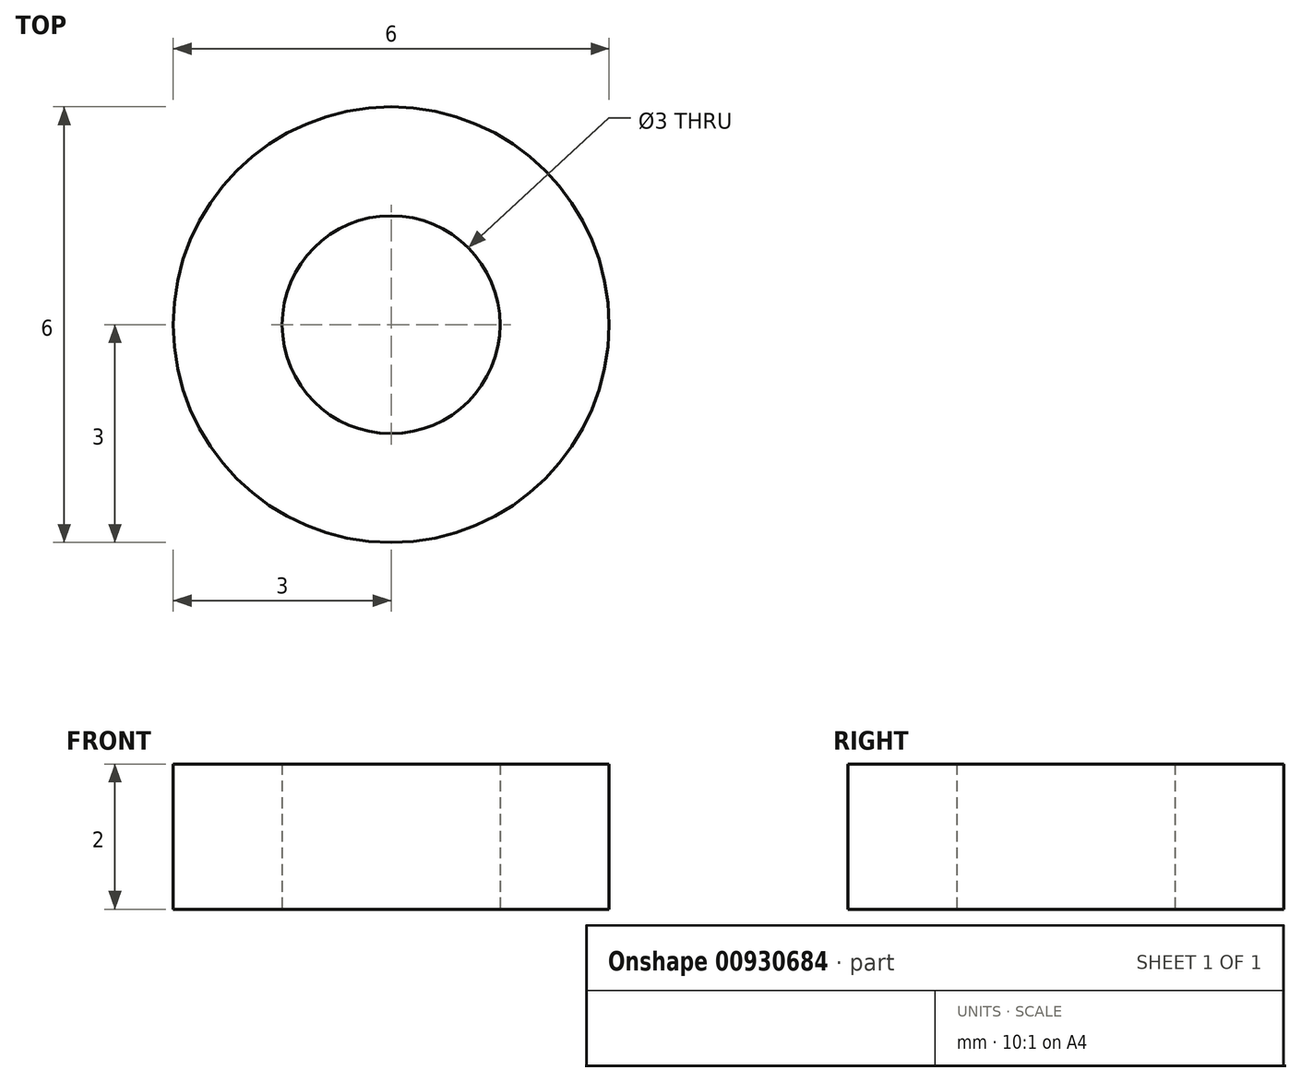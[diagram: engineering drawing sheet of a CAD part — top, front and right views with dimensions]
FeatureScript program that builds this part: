
annotation { "Feature Type Name" : "Feature", "Feature Type Description" : "" }
export const myFeature = defineFeature(function(context is Context, id is Id, definition is map)
    precondition{}
    {
        {
            var Q0;
            Q0=qCreatedBy(makeId("Top.planeOp"),FACE);
            var sketch = newSketch(context, id + "F0", { "sketchPlane" : qUnion([Q0])});
            skCircle(sketch, "E0", {"center": v(0, 0) * mm, "radius": 3 * mm});
            skCircle(sketch, "E1", {"center": v(0, 0) * mm, "radius": 1.5 * mm});
            skSolve(sketch);
        }
        {
            var Q0;
            Q0=qSketchRegion(id+"F0",true);
            extrude(context, id + "F1", {"entities" : qUnion([Q0]), "depth" : 2 * mm});
        }
    });
